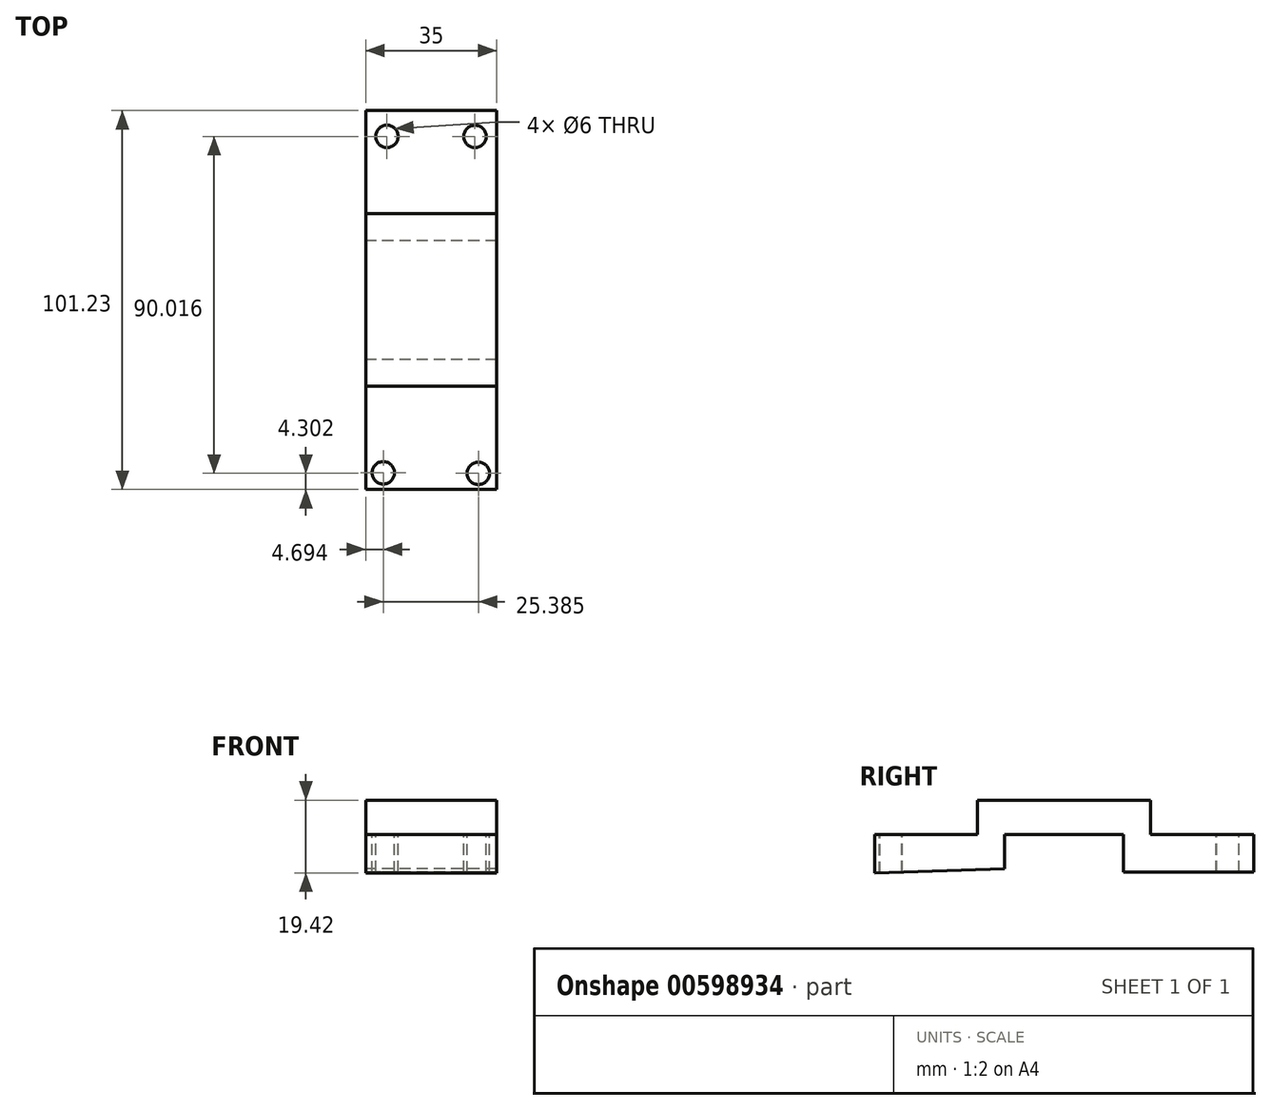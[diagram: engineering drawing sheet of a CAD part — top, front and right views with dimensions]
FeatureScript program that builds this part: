
annotation { "Feature Type Name" : "Feature", "Feature Type Description" : "" }
export const myFeature = defineFeature(function(context is Context, id is Id, definition is map)
    precondition{}
    {
        {
            var Q0;
            Q0=qCreatedBy(makeId("Right.planeOp"),FACE);
            var sketch = newSketch(context, id + "F0", { "sketchPlane" : qUnion([Q0])});
            skLineSegment(sketch, "E0.bottom", {"start": v(-18.1, 0) * mm, "end": v(-52.87, -1.14) * mm});
            skLineSegment(sketch, "E0.top", {"start": v(-25.34, 9.1) * mm, "end": v(-52.87, 9.1) * mm});
            skLineSegment(sketch, "E0.left", {"start": v(-18.1, 0) * mm, "end": v(-18.1, 9.1) * mm});
            skLineSegment(sketch, "E0.right", {"start": v(-52.87, -1.14) * mm, "end": v(-52.87, 9.1) * mm});
            skLineSegment(sketch, "E1.bottom", {"start": v(-18.1, 9.1) * mm, "end": v(13.6, 9.1) * mm});
            skLineSegment(sketch, "E1.top", {"start": v(-25.34, 18.28) * mm, "end": v(20.83, 18.28) * mm});
            skLineSegment(sketch, "E1.left", {"start": v(-25.34, 9.1) * mm, "end": v(-25.34, 18.28) * mm});
            skLineSegment(sketch, "E1.right", {"start": v(20.83, 9.1) * mm, "end": v(20.83, 18.28) * mm});
            skLineSegment(sketch, "E2.bottom", {"start": v(20.83, 9.1) * mm, "end": v(48.36, 9.1) * mm});
            skLineSegment(sketch, "E2.top", {"start": v(13.6, -0.9) * mm, "end": v(48.36, -0.9) * mm});
            skLineSegment(sketch, "E2.left", {"start": v(13.6, 9.1) * mm, "end": v(13.6, -0.9) * mm});
            skLineSegment(sketch, "E2.right", {"start": v(48.36, 9.1) * mm, "end": v(48.36, -0.9) * mm});
            skSolve(sketch);
        }
        {
            var Q0;
            Q0 = qSketchRegion(id + "F0", true);
            extrude(context, id + "F1", {"entities" : qUnion([Q0]), "endBound" : BoundingType.SYMMETRIC, "depth" : 35 * mm, "offsetDistance" : 25 * mm});
        }
        {
            var Q0;
            Q0=makeQuery(id+"F1.opExtrude","SWEPT_FACE",FACE,{"disambiguationData":[OSD([sQuery(id+"F0.wireOp",EDGE,"E2.bottom")])]});
            var sketch = newSketch(context, id + "F2", { "sketchPlane" : qUnion([Q0])});
            skCircle(sketch, "E3", {"center": v(11.68, 41.43) * mm, "radius": 3.81 * mm});
            skCircle(sketch, "E4", {"center": v(-11.84, 41.45) * mm, "radius": 3.92 * mm});
            skSolve(sketch);
        }
        {
            var Q0;
            Q0=makeQuery(id+"F1.opExtrude","SWEPT_FACE",FACE,{"disambiguationData":[OSD([sQuery(id+"F0.wireOp",EDGE,"E0.top")])]});
            var sketch = newSketch(context, id + "F3", { "sketchPlane" : qUnion([Q0])});
            skCircle(sketch, "E5", {"center": v(-12.8, -48.43) * mm, "radius": 3.14 * mm});
            skCircle(sketch, "E6", {"center": v(12.58, -48.57) * mm, "radius": 3.26 * mm});
            skSolve(sketch);
        }
        {
            var Q0;
            Q0=sQuery(id+"F3.wireOp",VERTEX,"E6.center");
            var Q1;
            Q1=sQuery(id+"F3.wireOp",VERTEX,"E5.center");
            var Q2;
            Q2=sQuery(id+"F2.wireOp",VERTEX,"E4.center");
            var Q3;
            Q3=sQuery(id+"F2.wireOp",VERTEX,"E3.center");
            var Q4;
            Q4=makeQuery(id+"F1.opExtrude","SWEPT_BODY",BODY,{"disambiguationData":[OSD([sQuery(id+"F0.wireOp",EDGE,"E0.bottom"),sQuery(id+"F0.wireOp",EDGE,"E0.top"),sQuery(id+"F0.wireOp",EDGE,"E0.left"),sQuery(id+"F0.wireOp",EDGE,"E0.right"),sQuery(id+"F0.wireOp",EDGE,"E1.bottom"),sQuery(id+"F0.wireOp",EDGE,"E1.top"),sQuery(id+"F0.wireOp",EDGE,"E1.left"),sQuery(id+"F0.wireOp",EDGE,"E1.right"),sQuery(id+"F0.wireOp",EDGE,"E2.bottom"),sQuery(id+"F0.wireOp",EDGE,"E2.top"),sQuery(id+"F0.wireOp",EDGE,"E2.left"),sQuery(id+"F0.wireOp",EDGE,"E2.right")])]});
            hole(context, id + "F4", {"style" : HoleStyle.SIMPLE, "endStyle" : HoleEndStyle.THROUGH, "holeDiameter" : 6 * mm, "majorDiameter" : 5 * mm, "isTappedThrough" : true, "tappedDepth" : 12 * mm, "tapClearance" : 3, "locations" : qUnion([Q0, Q1, Q2, Q3]), "scope" : qUnion([Q4])});
        }
    });
